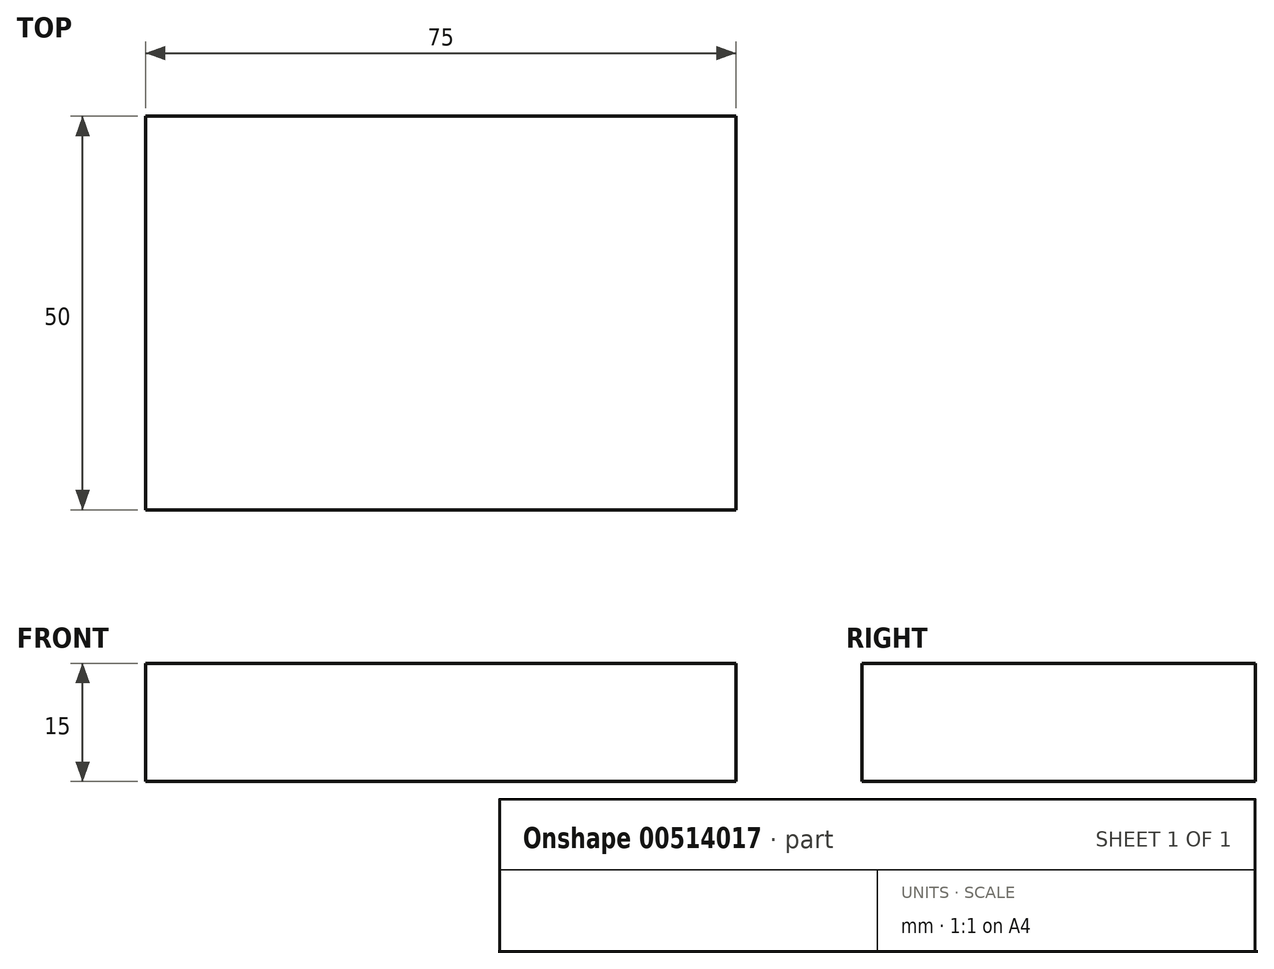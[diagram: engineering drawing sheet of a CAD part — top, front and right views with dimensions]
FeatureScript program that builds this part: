
annotation { "Feature Type Name" : "Feature", "Feature Type Description" : "" }
export const myFeature = defineFeature(function(context is Context, id is Id, definition is map)
    precondition{}
    {
        {
            var Q0;
            Q0=qCreatedBy(makeId("Top.planeOp"),FACE);
            var sketch = newSketch(context, id + "F0", { "sketchPlane" : qUnion([Q0])});
            skLineSegment(sketch, "E0.bottom", {"start": v(0, 0) * mm, "end": v(75, 0) * mm});
            skLineSegment(sketch, "E0.top", {"start": v(0, 50) * mm, "end": v(75, 50) * mm});
            skLineSegment(sketch, "E0.left", {"start": v(0, 0) * mm, "end": v(0, 50) * mm});
            skLineSegment(sketch, "E0.right", {"start": v(75, 0) * mm, "end": v(75, 50) * mm});
            skSolve(sketch);
        }
        {
            var Q0;
            Q0 = qSketchRegion(id + "F0", true);
            extrude(context, id + "F1", {"entities" : qUnion([Q0]), "depth" : 15 * mm});
        }
    });
